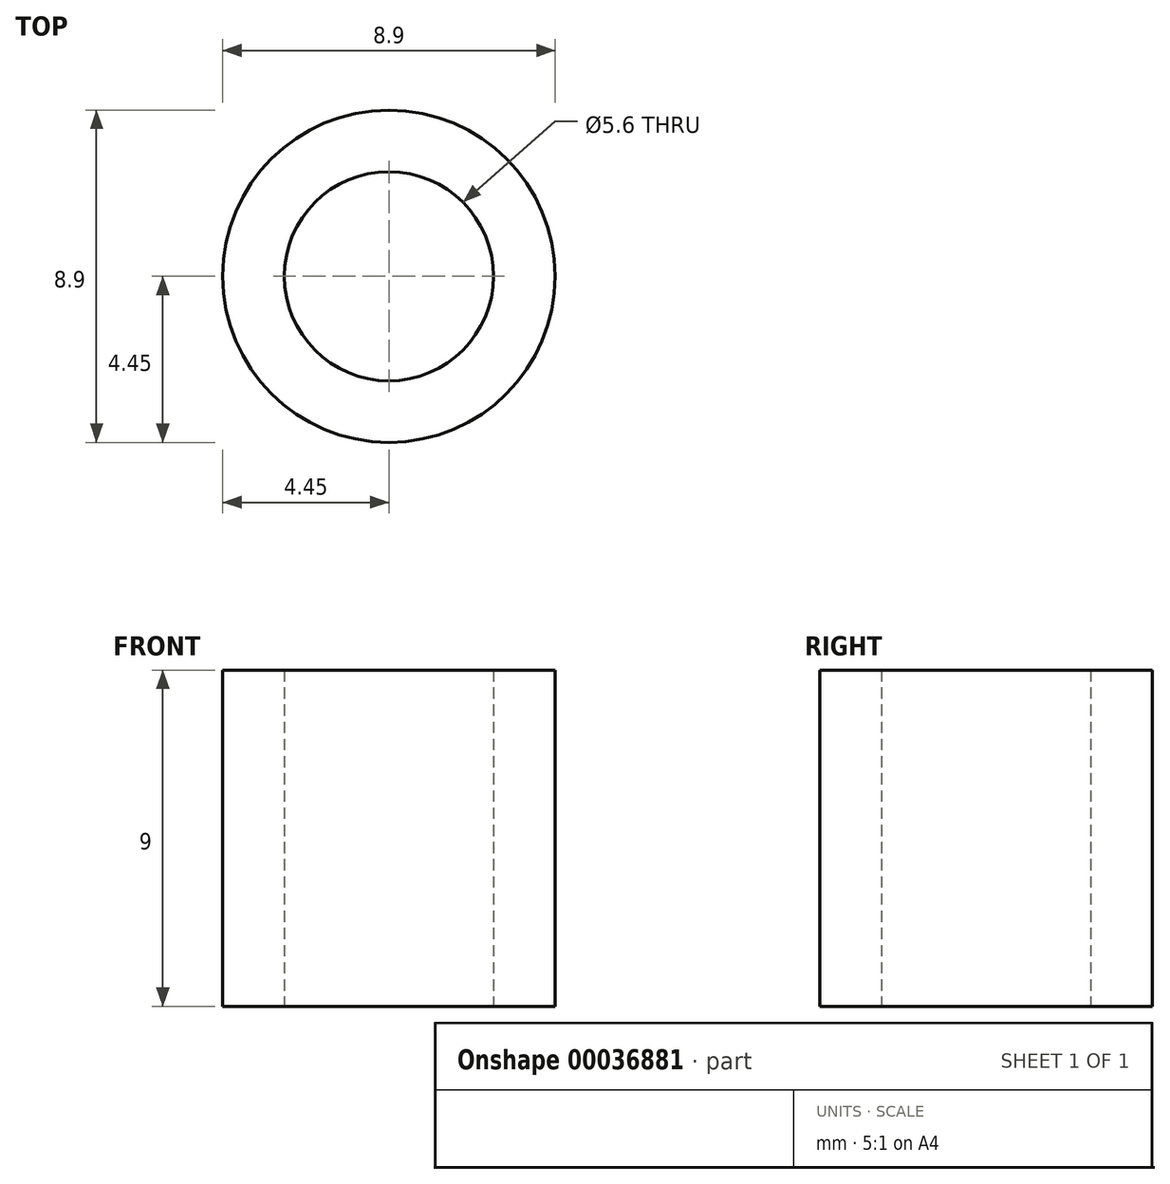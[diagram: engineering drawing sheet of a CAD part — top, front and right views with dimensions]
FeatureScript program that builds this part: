
annotation { "Feature Type Name" : "Feature", "Feature Type Description" : "" }
export const myFeature = defineFeature(function(context is Context, id is Id, definition is map)
    precondition{}
    {
        {
            var Q0;
            Q0=qCreatedBy(makeId("Top.planeOp"),FACE);
            var sketch = newSketch(context, id + "F0", { "sketchPlane" : qUnion([Q0])});
            skCircle(sketch, "E0", {"center": v(0, 0) * mm, "radius": 2.8 * mm});
            skCircle(sketch, "E1", {"center": v(0, 0) * mm, "radius": 4.45 * mm});
            skSolve(sketch);
        }
        {
            var Q0;
            Q0=makeQuery(id+"F0.imprint","IMPRINT",FACE,{"disambiguationData":[TD([[makeQuery(id+"F0.imprint","IMPRINT",EDGE,{"derivedFrom":sQuery(id+"F0.wireOp",EDGE,"E0")}),-1.0]])]});
            extrude(context, id + "F1", {"entities" : qUnion([Q0]), "depth" : 9 * mm});
        }
    });
